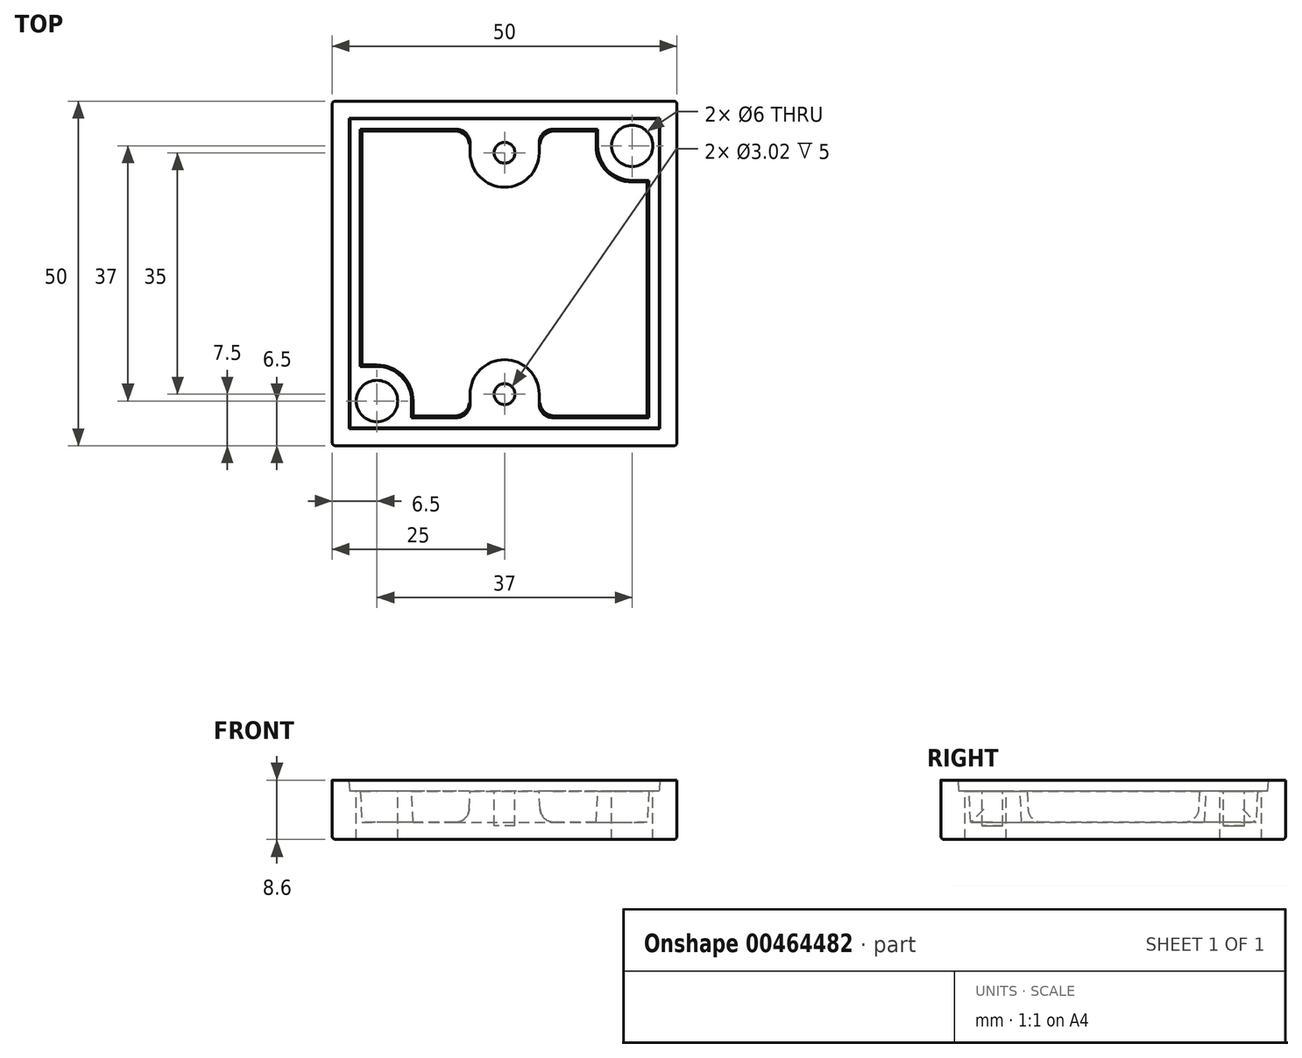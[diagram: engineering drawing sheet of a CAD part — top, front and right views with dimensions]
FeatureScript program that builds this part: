
annotation { "Feature Type Name" : "Feature", "Feature Type Description" : "" }
export const myFeature = defineFeature(function(context is Context, id is Id, definition is map)
    precondition{}
    {
        {
            var Q0;
            Q0=qCreatedBy(makeId("Top.planeOp"),FACE);
            var sketch = newSketch(context, id + "F0", { "sketchPlane" : qUnion([Q0])});
            skLineSegment(sketch, "E0.bottom", {"start": v(25, 25) * mm, "end": v(-25, 25) * mm});
            skLineSegment(sketch, "E0.top", {"start": v(25, -25) * mm, "end": v(-25, -25) * mm});
            skLineSegment(sketch, "E0.left", {"start": v(25, 25) * mm, "end": v(25, -25) * mm});
            skLineSegment(sketch, "E0.right", {"start": v(-25, 25) * mm, "end": v(-25, -25) * mm});
            skPoint(sketch, "E0.middle", {"position": v(0, 0) * mm});
            skSolve(sketch);
        }
        {
            var Q0;
            Q0=qSketchRegion(id+"F0",true);
            extrude(context, id + "F1", {"entities" : qUnion([Q0]), "oppositeDirection" : true, "depth" : 8.6 * mm});
        }
        {
            var Q0;
            Q0=makeQuery(id+"F1.opExtrude","CAP_FACE",FACE,{"disambiguationData":[OSD([sQuery(id+"F0.wireOp",EDGE,"E0.bottom"),sQuery(id+"F0.wireOp",EDGE,"E0.top"),sQuery(id+"F0.wireOp",EDGE,"E0.left"),sQuery(id+"F0.wireOp",EDGE,"E0.right")])],"isStart":true});
            var sketch = newSketch(context, id + "F2", { "sketchPlane" : qUnion([Q0])});
            skLineSegment(sketch, "E1.0", {"start": v(-22.5, 22.5) * mm, "end": v(-22.5, -22.5) * mm});
            skLineSegment(sketch, "E1.1", {"start": v(22.5, 22.5) * mm, "end": v(-22.5, 22.5) * mm});
            skLineSegment(sketch, "E1.2", {"start": v(22.5, 22.5) * mm, "end": v(22.5, -22.5) * mm});
            skLineSegment(sketch, "E1.3", {"start": v(22.5, -22.5) * mm, "end": v(-22.5, -22.5) * mm});
            skSolve(sketch);
        }
        {
            var Q0;
            Q0=qSketchRegion(id+"F2",true);
            extrude(context, id + "F3", {"entities" : qUnion([Q0]), "operationType" : NewBodyOperationType.REMOVE, "oppositeDirection" : true, "depth" : 1.6 * mm, "hasDraft" : true, "draftAngle" : 3 * degree, "draftPullDirection" : true});
        }
        {
            var Q0;
            Q0=makeQuery(id+"F3.boolean.opBoolean","COPY",FACE,{"derivedFrom":makeQuery(id+"F3.opExtrude","CAP_FACE",FACE,{"disambiguationData":[OSD([sQuery(id+"F2.wireOp",EDGE,"E1.0"),sQuery(id+"F2.wireOp",EDGE,"E1.1"),sQuery(id+"F2.wireOp",EDGE,"E1.2"),sQuery(id+"F2.wireOp",EDGE,"E1.3")])],"isStart":false})});
            var sketch = newSketch(context, id + "F4", { "sketchPlane" : qUnion([Q0])});
            skLineSegment(sketch, "E2.0", {"start": v(13.5, 20.92) * mm, "end": v(5, 20.92) * mm});
            skLineSegment(sketch, "E2.1", {"start": v(20.92, 13.5) * mm, "end": v(20.92, -20.92) * mm});
            skLineSegment(sketch, "E3", {"start": v(0, 0) * mm, "end": v(20.92, 20.92) * mm, "construction": true});
            skArc(sketch, "E4", {"start": v(13.5, 18.5) * mm, "mid": v(14.96, 14.96) * mm, "end": v(18.5, 13.5) * mm});
            skLineSegment(sketch, "E5", {"start": v(13.5, 18.5) * mm, "end": v(13.5, 20.92) * mm});
            skLineSegment(sketch, "E6", {"start": v(18.5, 13.5) * mm, "end": v(20.92, 13.5) * mm});
            skLineSegment(sketch, "E7", {"start": v(-22.42, 22.42) * mm, "end": v(22.42, -22.42) * mm, "construction": true});
            skLineSegment(sketch, "E8.MirrorCS", {"start": v(-18.5, -13.5) * mm, "end": v(-20.92, -13.5) * mm});
            skLineSegment(sketch, "E9.MirrorCS", {"start": v(-20.92, -13.5) * mm, "end": v(-20.92, 20.92) * mm});
            skLineSegment(sketch, "E10.MirrorCS", {"start": v(-13.5, -20.92) * mm, "end": v(-5, -20.92) * mm});
            skLineSegment(sketch, "E11.MirrorCS", {"start": v(-13.5, -18.5) * mm, "end": v(-13.5, -20.92) * mm});
            skArc(sketch, "E12.MirrorCS", {"start": v(-18.5, -13.5) * mm, "mid": v(-14.96, -14.96) * mm, "end": v(-13.5, -18.5) * mm});
            skArc(sketch, "E13", {"start": v(-5, 17.5) * mm, "mid": v(0, 12.5) * mm, "end": v(5, 17.5) * mm});
            skLineSegment(sketch, "E14", {"start": v(-5, 20.92) * mm, "end": v(-5, 17.5) * mm});
            skLineSegment(sketch, "E15", {"start": v(5, 20.92) * mm, "end": v(5, 17.5) * mm});
            skLineSegment(sketch, "E16.trimOffspring", {"start": v(-5, 20.92) * mm, "end": v(-20.92, 20.92) * mm});
            skArc(sketch, "E17.MirrorCS", {"start": v(-5, -17.5) * mm, "mid": v(0, -12.5) * mm, "end": v(5, -17.5) * mm});
            skLineSegment(sketch, "E18.MirrorCS", {"start": v(5, -20.92) * mm, "end": v(5, -17.5) * mm});
            skLineSegment(sketch, "E19.MirrorCS", {"start": v(-5, -20.92) * mm, "end": v(-5, -17.5) * mm});
            skLineSegment(sketch, "E20.trimOffspring", {"start": v(5, -20.92) * mm, "end": v(20.92, -20.92) * mm});
            skSolve(sketch);
        }
        {
            var Q0;
            Q0=qSketchRegion(id+"F4",true);
            extrude(context, id + "F5", {"entities" : qUnion([Q0]), "operationType" : NewBodyOperationType.REMOVE, "oppositeDirection" : true, "depth" : 4.5 * mm, "hasDraft" : true, "draftAngle" : 3 * degree, "draftPullDirection" : true});
        }
        {
            var Q0;
            Q0=makeQuery(id+"F3.boolean.opBoolean","COPY",FACE,{"derivedFrom":makeQuery(id+"F3.opExtrude","CAP_FACE",FACE,{"disambiguationData":[OSD([sQuery(id+"F2.wireOp",EDGE,"E1.0"),sQuery(id+"F2.wireOp",EDGE,"E1.1"),sQuery(id+"F2.wireOp",EDGE,"E1.2"),sQuery(id+"F2.wireOp",EDGE,"E1.3")])],"isStart":false})});
            var sketch = newSketch(context, id + "F6", { "sketchPlane" : qUnion([Q0])});
            skCircle(sketch, "E21", {"center": v(18.5, 18.5) * mm, "radius": 3 * mm});
            skCircle(sketch, "E22", {"center": v(-18.5, -18.5) * mm, "radius": 3 * mm});
            skPoint(sketch, "E23.center.orphan", {"position": v(0, 17.5) * mm});
            skPoint(sketch, "E24.center.orphan", {"position": v(0, -17.5) * mm});
            skSolve(sketch);
        }
        {
            var Q0;
            Q0=qSketchRegion(id+"F6",true);
            extrude(context, id + "F7", {"entities" : qUnion([Q0]), "operationType" : NewBodyOperationType.REMOVE, "endBound" : BoundingType.UP_TO_NEXT, "oppositeDirection" : true, "depth" : 25 * mm});
        }
        {
            var Q0;
            Q0=makeQuery(id+"F1.opExtrude","CAP_EDGE",EDGE,{"disambiguationData":[OSD([sQuery(id+"F0.wireOp",EDGE,"E0.top")])],"isStart":false});
            var Q1;
            Q1=makeQuery(id+"F1.opExtrude","SWEPT_EDGE",EDGE,{"disambiguationData":[OSD([sQuery(id+"F0.wireOp",EDGE,"E0.top"),sQuery(id+"F0.wireOp",EDGE,"E0.right")])]});
            var Q2;
            Q2=makeQuery(id+"F1.opExtrude","CAP_EDGE",EDGE,{"disambiguationData":[OSD([sQuery(id+"F0.wireOp",EDGE,"E0.right")])],"isStart":false});
            var Q3;
            Q3=makeQuery(id+"F7.boolean.opBoolean","COPY",EDGE,{"derivedFrom":makeQuery(id+"F7.opExtrude","TWEAK_EDGE",EDGE,{"derivedFrom":[makeQuery(id+"F1.opExtrude","CAP_FACE",FACE,{"disambiguationData":[OSD([sQuery(id+"F0.wireOp",EDGE,"E0.bottom"),sQuery(id+"F0.wireOp",EDGE,"E0.top"),sQuery(id+"F0.wireOp",EDGE,"E0.left"),sQuery(id+"F0.wireOp",EDGE,"E0.right")])],"isStart":false}),makeQuery(id+"F6.imprint","IMPRINT",EDGE,{"derivedFrom":sQuery(id+"F6.wireOp",EDGE,"E22")})]})});
            var Q4;
            Q4=makeQuery(id+"F7.boolean.opBoolean","COPY",EDGE,{"derivedFrom":makeQuery(id+"F7.opExtrude","TWEAK_EDGE",EDGE,{"derivedFrom":[makeQuery(id+"F1.opExtrude","CAP_FACE",FACE,{"disambiguationData":[OSD([sQuery(id+"F0.wireOp",EDGE,"E0.bottom"),sQuery(id+"F0.wireOp",EDGE,"E0.top"),sQuery(id+"F0.wireOp",EDGE,"E0.left"),sQuery(id+"F0.wireOp",EDGE,"E0.right")])],"isStart":false}),makeQuery(id+"F6.imprint","IMPRINT",EDGE,{"derivedFrom":sQuery(id+"F6.wireOp",EDGE,"E21")})]})});
            var Q5;
            Q5=makeQuery(id+"F1.opExtrude","SWEPT_EDGE",EDGE,{"disambiguationData":[OSD([sQuery(id+"F0.wireOp",EDGE,"E0.bottom"),sQuery(id+"F0.wireOp",EDGE,"E0.right")])]});
            var Q6;
            Q6=makeQuery(id+"F1.opExtrude","CAP_EDGE",EDGE,{"disambiguationData":[OSD([sQuery(id+"F0.wireOp",EDGE,"E0.bottom")])],"isStart":false});
            var Q7;
            Q7=makeQuery(id+"F1.opExtrude","SWEPT_EDGE",EDGE,{"disambiguationData":[OSD([sQuery(id+"F0.wireOp",EDGE,"E0.bottom"),sQuery(id+"F0.wireOp",EDGE,"E0.left")])]});
            var Q8;
            Q8=makeQuery(id+"F1.opExtrude","CAP_EDGE",EDGE,{"disambiguationData":[OSD([sQuery(id+"F0.wireOp",EDGE,"E0.left")])],"isStart":false});
            var Q9;
            Q9=makeQuery(id+"F1.opExtrude","SWEPT_EDGE",EDGE,{"disambiguationData":[OSD([sQuery(id+"F0.wireOp",EDGE,"E0.top"),sQuery(id+"F0.wireOp",EDGE,"E0.left")])]});
            fillet(context, id + "F8", {"entities" : qUnion([Q0, Q1, Q2, Q3, Q4, Q5, Q6, Q7, Q8, Q9]), "radius" : 0.5 * mm, "tangentPropagation" : true, "allowEdgeOverflow" : false});
        }
        {
            var Q0;
            Q0=makeQuery(id+"F3.boolean.opBoolean","COPY",FACE,{"derivedFrom":makeQuery(id+"F3.opExtrude","CAP_FACE",FACE,{"disambiguationData":[OSD([sQuery(id+"F2.wireOp",EDGE,"E1.0"),sQuery(id+"F2.wireOp",EDGE,"E1.1"),sQuery(id+"F2.wireOp",EDGE,"E1.2"),sQuery(id+"F2.wireOp",EDGE,"E1.3")])],"isStart":false})});
            var sketch = newSketch(context, id + "F9", { "sketchPlane" : qUnion([Q0])});
            skCircle(sketch, "E25", {"center": v(0, 17.5) * mm, "radius": 1.5 * mm});
            skCircle(sketch, "E26", {"center": v(0, -17.5) * mm, "radius": 1.5 * mm});
            skPoint(sketch, "E27.0.end.orphan", {"position": v(5, -17.5) * mm});
            skPoint(sketch, "E27.0.start.orphan", {"position": v(-5, -17.5) * mm});
            skPoint(sketch, "E28.0.end.orphan", {"position": v(5.24, 17.5) * mm});
            skPoint(sketch, "E28.0.start.orphan", {"position": v(-5.24, 17.5) * mm});
            skSolve(sketch);
        }
        {
            var Q0;
            Q0 = qSketchRegion(id + "F9", true);
            extrude(context, id + "F10", {"entities" : qUnion([Q0]), "operationType" : NewBodyOperationType.REMOVE, "oppositeDirection" : true, "depth" : 5 * mm});
        }
        {
            var Q0;
            Q0=makeQuery(id+"F5.boolean.opBoolean","COPY",EDGE,{"derivedFrom":makeQuery(id+"F5.opExtrude","SWEPT_EDGE",EDGE,{"disambiguationData":[OSD([sQuery(id+"F4.wireOp",EDGE,"E2.0"),sQuery(id+"F4.wireOp",EDGE,"E15")])]})});
            var Q1;
            Q1=makeQuery(id+"F5.boolean.opBoolean","COPY",EDGE,{"derivedFrom":makeQuery(id+"F5.opExtrude","CAP_EDGE",EDGE,{"disambiguationData":[OSD([sQuery(id+"F4.wireOp",EDGE,"E13")])],"isStart":false})});
            var Q2;
            Q2=makeQuery(id+"F5.boolean.opBoolean","COPY",EDGE,{"derivedFrom":makeQuery(id+"F5.opExtrude","SWEPT_EDGE",EDGE,{"disambiguationData":[OSD([sQuery(id+"F4.wireOp",EDGE,"E14"),sQuery(id+"F4.wireOp",EDGE,"E16.trimOffspring")])]})});
            var Q3;
            Q3=makeQuery(id+"F5.boolean.opBoolean","COPY",EDGE,{"derivedFrom":makeQuery(id+"F5.opExtrude","SWEPT_EDGE",EDGE,{"disambiguationData":[OSD([sQuery(id+"F4.wireOp",EDGE,"E10.MirrorCS"),sQuery(id+"F4.wireOp",EDGE,"E19.MirrorCS")])]})});
            var Q4;
            Q4=makeQuery(id+"F5.boolean.opBoolean","COPY",EDGE,{"derivedFrom":makeQuery(id+"F5.opExtrude","CAP_EDGE",EDGE,{"disambiguationData":[OSD([sQuery(id+"F4.wireOp",EDGE,"E19.MirrorCS")])],"isStart":false})});
            var Q5;
            Q5=makeQuery(id+"F5.boolean.opBoolean","COPY",EDGE,{"derivedFrom":makeQuery(id+"F5.opExtrude","SWEPT_EDGE",EDGE,{"disambiguationData":[OSD([sQuery(id+"F4.wireOp",EDGE,"E18.MirrorCS"),sQuery(id+"F4.wireOp",EDGE,"E20.trimOffspring")])]})});
            fillet(context, id + "F11", {"entities" : qUnion([Q0, Q1, Q2, Q3, Q4, Q5]), "radius" : 2 * mm, "tangentPropagation" : true, "allowEdgeOverflow" : false});
        }
    });
